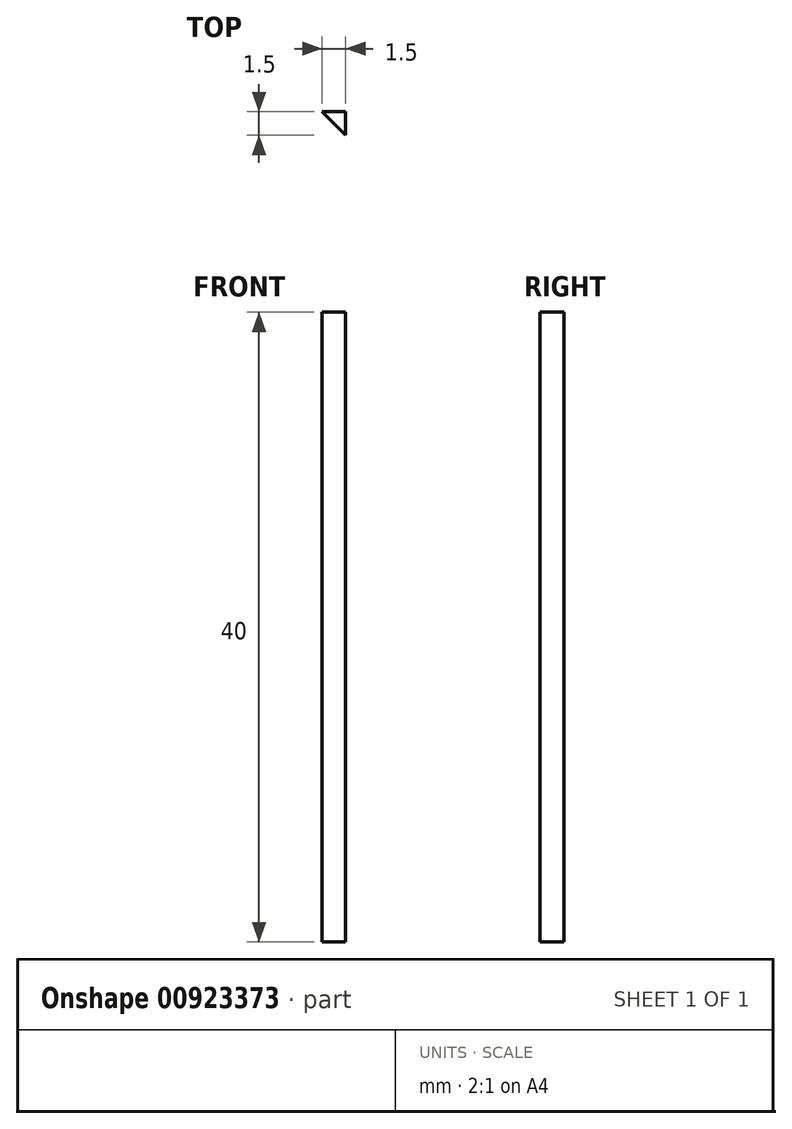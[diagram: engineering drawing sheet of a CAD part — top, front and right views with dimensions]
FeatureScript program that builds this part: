
annotation { "Feature Type Name" : "Feature", "Feature Type Description" : "" }
export const myFeature = defineFeature(function(context is Context, id is Id, definition is map)
    precondition{}
    {
        {
            var Q0;
            Q0=qCreatedBy(makeId("Front.planeOp"),FACE);
            var sketch = newSketch(context, id + "F0", { "sketchPlane" : qUnion([Q0])});
            skLineSegment(sketch, "E0.bottom", {"start": v(1.25, -20) * mm, "end": v(-1.25, -20) * mm});
            skLineSegment(sketch, "E0.top", {"start": v(1.25, 20) * mm, "end": v(-1.25, 20) * mm});
            skLineSegment(sketch, "E0.left", {"start": v(1.25, -20) * mm, "end": v(1.25, 20) * mm});
            skLineSegment(sketch, "E0.right", {"start": v(-1.25, -20) * mm, "end": v(-1.25, 20) * mm});
            skPoint(sketch, "E0.middle", {"position": v(0, 0) * mm});
            skSolve(sketch);
        }
        {
            var Q0;
            Q0 = qSketchRegion(id + "F0", true);
            extrude(context, id + "F1", {"entities" : qUnion([Q0]), "depth" : 2 * mm, "offsetDistance" : 25 * mm});
        }
        {
            var Q0;
            Q0=makeQuery(id+"F1.opExtrude","CAP_EDGE",EDGE,{"disambiguationData":[OSD([sQuery(id+"F0.wireOp",EDGE,"E0.right")])],"isStart":false});
            chamfer(context, id + "F2", {"entities" : qUnion([Q0]), "width" : 3 * mm, "tangentPropagation" : true});
        }
    });
